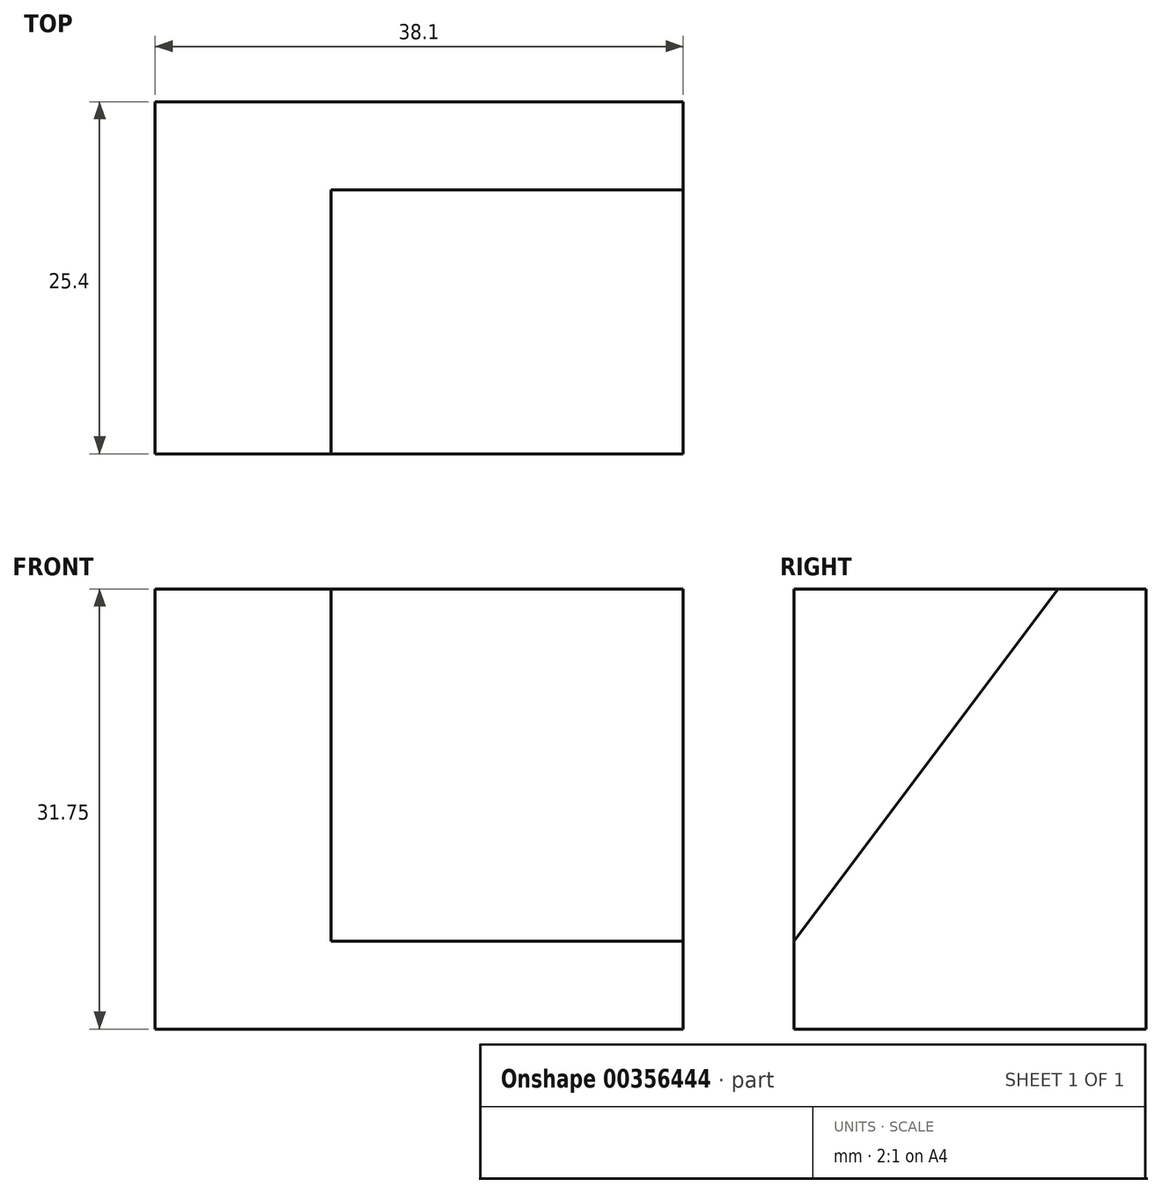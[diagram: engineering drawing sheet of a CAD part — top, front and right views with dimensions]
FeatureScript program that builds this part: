
annotation { "Feature Type Name" : "Feature", "Feature Type Description" : "" }
export const myFeature = defineFeature(function(context is Context, id is Id, definition is map)
    precondition{}
    {
        {
            var Q0;
            Q0=qCreatedBy(makeId("Right.planeOp"),FACE);
            var sketch = newSketch(context, id + "F0", { "sketchPlane" : qUnion([Q0])});
            skLineSegment(sketch, "E0", {"start": v(0, 0) * mm, "end": v(0, 31.75) * mm});
            skLineSegment(sketch, "E1", {"start": v(0, 31.75) * mm, "end": v(25.4, 31.75) * mm});
            skLineSegment(sketch, "E2", {"start": v(25.4, 31.75) * mm, "end": v(25.4, 0) * mm});
            skLineSegment(sketch, "E3", {"start": v(25.4, 0) * mm, "end": v(0, 0) * mm});
            skSolve(sketch);
        }
        {
            var Q0;
            Q0 = qSketchRegion(id + "F0", true);
            extrude(context, id + "F1", {"entities" : qUnion([Q0]), "depth" : 38.1 * mm});
        }
        {
            var Q0;
            Q0=makeQuery(id+"F1.opExtrude","CAP_FACE",FACE,{"disambiguationData":[OSD([sQuery(id+"F0.wireOp",EDGE,"E0"),sQuery(id+"F0.wireOp",EDGE,"E1"),sQuery(id+"F0.wireOp",EDGE,"E2"),sQuery(id+"F0.wireOp",EDGE,"E3")])],"isStart":false});
            var sketch = newSketch(context, id + "F2", { "sketchPlane" : qUnion([Q0])});
            skLineSegment(sketch, "E4", {"start": v(19.05, 31.75) * mm, "end": v(0, 6.35) * mm});
            skLineSegment(sketch, "E5", {"start": v(0, 6.35) * mm, "end": v(0, 31.75) * mm});
            skLineSegment(sketch, "E6", {"start": v(0, 31.75) * mm, "end": v(19.05, 31.75) * mm});
            skSolve(sketch);
        }
        {
            var Q0;
            Q0 = qSketchRegion(id + "F2", true);
            extrude(context, id + "F3", {"entities" : qUnion([Q0]), "operationType" : NewBodyOperationType.REMOVE, "oppositeDirection" : true, "depth" : 25.4 * mm});
        }
    });
